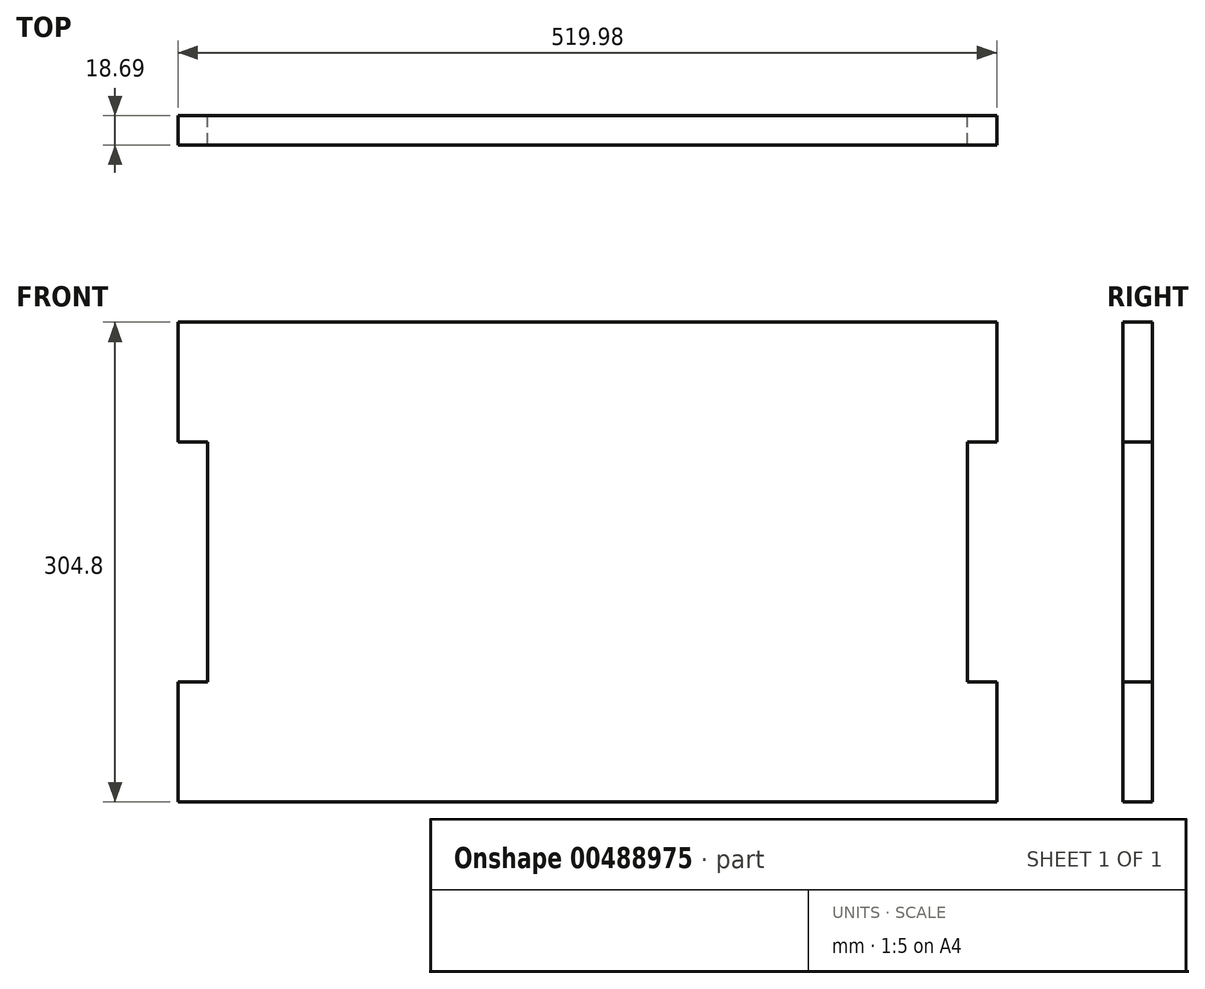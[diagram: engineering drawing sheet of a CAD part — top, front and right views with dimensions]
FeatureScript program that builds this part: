
annotation { "Feature Type Name" : "Feature", "Feature Type Description" : "" }
export const myFeature = defineFeature(function(context is Context, id is Id, definition is map)
    precondition{}
    {
        {
            var Q0;
            Q0=qCreatedBy(makeId("Front.planeOp"),FACE);
            var sketch = newSketch(context, id + "F0", { "sketchPlane" : qUnion([Q0])});
            skLineSegment(sketch, "E0.bottom", {"start": v(-303.66, -113.34) * mm, "end": v(178.94, -113.34) * mm});
            skLineSegment(sketch, "E0.top", {"start": v(-303.66, 191.46) * mm, "end": v(178.94, 191.46) * mm});
            skLineSegment(sketch, "E0.left", {"start": v(-303.66, -113.34) * mm, "end": v(-303.66, 191.46) * mm});
            skLineSegment(sketch, "E0.right", {"start": v(178.94, -113.34) * mm, "end": v(178.94, 191.46) * mm});
            skLineSegment(sketch, "E1.bottom", {"start": v(-303.66, 191.46) * mm, "end": v(-322.35, 191.46) * mm});
            skLineSegment(sketch, "E1.top", {"start": v(-303.66, 115.26) * mm, "end": v(-322.35, 115.26) * mm});
            skLineSegment(sketch, "E1.left", {"start": v(-303.66, 191.46) * mm, "end": v(-303.66, 115.26) * mm});
            skLineSegment(sketch, "E1.right", {"start": v(-322.35, 191.46) * mm, "end": v(-322.35, 115.26) * mm});
            skLineSegment(sketch, "E2.bottom", {"start": v(-303.66, -113.34) * mm, "end": v(-322.35, -113.34) * mm});
            skLineSegment(sketch, "E2.top", {"start": v(-303.66, -37.14) * mm, "end": v(-322.35, -37.14) * mm});
            skLineSegment(sketch, "E2.left", {"start": v(-303.66, -113.34) * mm, "end": v(-303.66, -37.14) * mm});
            skLineSegment(sketch, "E2.right", {"start": v(-322.35, -113.34) * mm, "end": v(-322.35, -37.14) * mm});
            skLineSegment(sketch, "E3.bottom", {"start": v(178.94, 191.46) * mm, "end": v(197.63, 191.46) * mm});
            skLineSegment(sketch, "E3.top", {"start": v(178.94, 115.26) * mm, "end": v(197.63, 115.26) * mm});
            skLineSegment(sketch, "E3.left", {"start": v(178.94, 191.46) * mm, "end": v(178.94, 115.26) * mm});
            skLineSegment(sketch, "E3.right", {"start": v(197.63, 191.46) * mm, "end": v(197.63, 115.26) * mm});
            skLineSegment(sketch, "E4.bottom", {"start": v(178.94, -113.34) * mm, "end": v(197.63, -113.34) * mm});
            skLineSegment(sketch, "E4.top", {"start": v(178.94, -37.14) * mm, "end": v(197.63, -37.14) * mm});
            skLineSegment(sketch, "E4.left", {"start": v(178.94, -113.34) * mm, "end": v(178.94, -37.14) * mm});
            skLineSegment(sketch, "E4.right", {"start": v(197.63, -113.34) * mm, "end": v(197.63, -37.14) * mm});
            skSolve(sketch);
        }
        {
            var Q0;
            Q0=makeQuery(id+"F0.imprint","IMPRINT",FACE,{"disambiguationData":[TD([[makeQuery(id+"F0.imprint","IMPRINT",EDGE,{"derivedFrom":sQuery(id+"F0.wireOp",EDGE,"E1.bottom")}),1.0]])]});
            var Q1;
            Q1=makeQuery(id+"F0.imprint","IMPRINT",FACE,{"disambiguationData":[TD([[makeQuery(id+"F0.imprint","IMPRINT",EDGE,{"derivedFrom":sQuery(id+"F0.wireOp",EDGE,"E2.bottom")}),-1.0]])]});
            var Q2;
            Q2=makeQuery(id+"F0.imprint","IMPRINT",FACE,{"disambiguationData":[TD([[makeQuery(id+"F0.imprint","IMPRINT",EDGE,{"derivedFrom":sQuery(id+"F0.wireOp",EDGE,"E3.bottom")}),-1.0]])]});
            var Q3;
            Q3=makeQuery(id+"F0.imprint","IMPRINT",FACE,{"disambiguationData":[TD([[makeQuery(id+"F0.imprint","IMPRINT",EDGE,{"derivedFrom":sQuery(id+"F0.wireOp",EDGE,"E4.bottom")}),1.0]])]});
            var Q4;
            Q4=makeQuery(id+"F0.imprint","IMPRINT",FACE,{"disambiguationData":[TD([[makeQuery(id+"F0.imprint","IMPRINT",EDGE,{"derivedFrom":sQuery(id+"F0.wireOp",EDGE,"E0.bottom")}),1.0]])]});
            extrude(context, id + "F1", {"entities" : qUnion([Q0, Q1, Q2, Q3, Q4]), "depth" : 18.7 * mm, "offsetDistance" : 25.4 * mm});
        }
    });
